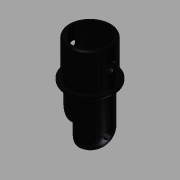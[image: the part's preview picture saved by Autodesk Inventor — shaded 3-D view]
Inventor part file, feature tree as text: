
AUTODESK INVENTOR PART (.ipt)
format: ipt  version: 2014 (Build 180170000, 170)  size: 310,272 bytes
history: native  units: mm
features: fillet x7, extrude x5, sketch x5
ambient origin geometry x8: Origin, YZ Plane, XZ Plane, XY Plane, X Axis, Y Axis, Z Axis, Center Point
bodies: Solid1 (feature_tree)
feature tree (17):
  extrude  "Extrusion1"  Depth=2.0mm TaperAngle=0.0deg
  extrude  "Extrusion2"  Depth=19.0mm
  extrude  "Extrusion3"  Depth=10.0mm
  fillet  "Fillet1"  Radius=20.0mm
  extrude  "Extrusion4"  Depth=10.0mm
  fillet  "Fillet2"  Radius=5.0mm
  fillet  "Fillet3"  Radius=20.0mm
  fillet  "Fillet4"  Radius=9.5mm
  fillet  "Fillet5"  Radius=20.0mm
  fillet  "Fillet6"  Radius=20.0mm
  extrude  "Extrusion5"  Depth=1.0mm
  fillet  "Fillet7"  Radius=1.0mm
  sketch  "Sketch1"  dims[d0=26.5mm d1=2.0mm d2=0.0mm]
  sketch  "Sketch2"  dims[d3=22.8mm d4=19.0mm]
  sketch  "Sketch4"  dims[d5=20.0mm d6=0.0mm d7=10.0mm d8=20.0mm]
  sketch  "Sketch5"  dims[d9=30.0mm d10=10.0mm d11=5.0mm d12=20.0mm d13=0.0mm d14=9.5mm d15=20.0mm d16=20.0mm d17=0.0mm]
  sketch  "Sketch6"  dims[d18=1.0mm d19=1.0mm d20=1.0mm d21=1.0mm d22=4.0mm d23=10.0mm d24=5.0mm d25=40.0mm d26=0.0mm d27=0.5mm]
